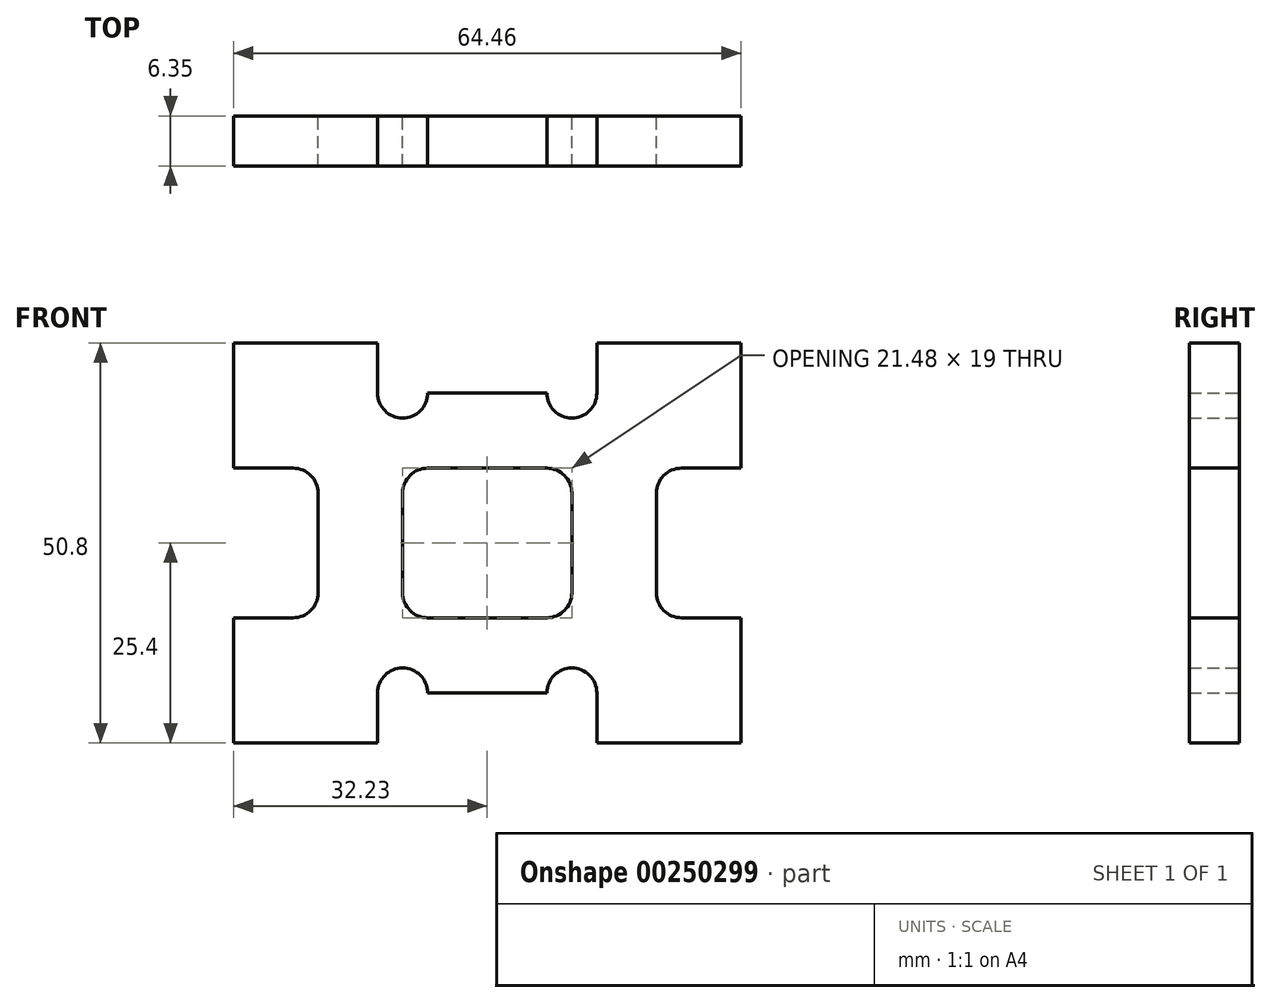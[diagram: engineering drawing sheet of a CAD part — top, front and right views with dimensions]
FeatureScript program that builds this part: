
annotation { "Feature Type Name" : "Feature", "Feature Type Description" : "" }
export const myFeature = defineFeature(function(context is Context, id is Id, definition is map)
    precondition{}
    {
        {
            var Q0;
            Q0=qCreatedBy(makeId("Front.planeOp"),FACE);
            var sketch = newSketch(context, id + "F0", { "sketchPlane" : qUnion([Q0])});
            skLineSegment(sketch, "E0", {"start": v(-13.92, -19.05) * mm, "end": v(-13.92, -25.4) * mm});
            skArc(sketch, "E1", {"start": v(-7.57, -19.05) * mm, "mid": v(-10.74, -15.88) * mm, "end": v(-13.92, -19.05) * mm});
            skLineSegment(sketch, "E2", {"start": v(7.57, -19.05) * mm, "end": v(-7.57, -19.05) * mm});
            skArc(sketch, "E3", {"start": v(13.92, -19.05) * mm, "mid": v(10.74, -15.88) * mm, "end": v(7.57, -19.05) * mm});
            skLineSegment(sketch, "E4", {"start": v(13.92, -25.4) * mm, "end": v(13.92, -19.05) * mm});
            skLineSegment(sketch, "E5", {"start": v(32.23, -25.4) * mm, "end": v(13.92, -25.4) * mm});
            skLineSegment(sketch, "E6", {"start": v(32.23, -9.5) * mm, "end": v(32.23, -25.4) * mm});
            skLineSegment(sketch, "E7", {"start": v(24.66, -9.5) * mm, "end": v(32.23, -9.5) * mm});
            skArc(sketch, "E8", {"start": v(21.48, -6.32) * mm, "mid": v(22.41, -8.57) * mm, "end": v(24.66, -9.5) * mm});
            skArc(sketch, "E9", {"start": v(24.66, 9.5) * mm, "mid": v(22.41, 8.57) * mm, "end": v(21.48, 6.32) * mm});
            skLineSegment(sketch, "E10", {"start": v(32.23, 9.5) * mm, "end": v(24.66, 9.5) * mm});
            skLineSegment(sketch, "E11", {"start": v(32.23, 25.4) * mm, "end": v(32.23, 9.5) * mm});
            skLineSegment(sketch, "E12", {"start": v(13.92, 25.4) * mm, "end": v(32.23, 25.4) * mm});
            skLineSegment(sketch, "E13", {"start": v(13.92, 19.05) * mm, "end": v(13.92, 25.4) * mm});
            skArc(sketch, "E14", {"start": v(7.57, 19.05) * mm, "mid": v(10.74, 15.88) * mm, "end": v(13.92, 19.05) * mm});
            skLineSegment(sketch, "E15", {"start": v(-7.57, 19.05) * mm, "end": v(7.57, 19.05) * mm});
            skArc(sketch, "E16", {"start": v(-13.92, 19.05) * mm, "mid": v(-10.74, 15.88) * mm, "end": v(-7.57, 19.05) * mm});
            skLineSegment(sketch, "E17", {"start": v(-13.92, 25.4) * mm, "end": v(-13.92, 19.05) * mm});
            skLineSegment(sketch, "E18", {"start": v(-32.23, 25.4) * mm, "end": v(-13.92, 25.4) * mm});
            skLineSegment(sketch, "E19", {"start": v(-32.23, 9.5) * mm, "end": v(-32.23, 25.4) * mm});
            skLineSegment(sketch, "E20", {"start": v(-32.23, -25.4) * mm, "end": v(-32.23, -9.5) * mm});
            skLineSegment(sketch, "E21", {"start": v(-13.92, -25.4) * mm, "end": v(-32.23, -25.4) * mm});
            skLineSegment(sketch, "E22", {"start": v(7.57, 9.5) * mm, "end": v(-7.57, 9.5) * mm});
            skLineSegment(sketch, "E23", {"start": v(-7.57, -9.5) * mm, "end": v(7.57, -9.5) * mm});
            skArc(sketch, "E24", {"start": v(-10.74, -6.32) * mm, "mid": v(-9.81, -8.57) * mm, "end": v(-7.57, -9.5) * mm});
            skArc(sketch, "E25", {"start": v(7.57, -9.5) * mm, "mid": v(9.81, -8.57) * mm, "end": v(10.74, -6.32) * mm});
            skArc(sketch, "E26", {"start": v(10.74, 6.32) * mm, "mid": v(9.81, 8.57) * mm, "end": v(7.57, 9.5) * mm});
            skArc(sketch, "E27", {"start": v(-7.57, 9.5) * mm, "mid": v(-9.81, 8.57) * mm, "end": v(-10.74, 6.32) * mm});
            skLineSegment(sketch, "E28", {"start": v(-24.66, -9.5) * mm, "end": v(-32.23, -9.5) * mm});
            skLineSegment(sketch, "E29", {"start": v(-32.23, 9.5) * mm, "end": v(-24.66, 9.5) * mm});
            skArc(sketch, "E30", {"start": v(-24.66, -9.5) * mm, "mid": v(-22.41, -8.57) * mm, "end": v(-21.48, -6.32) * mm});
            skArc(sketch, "E31", {"start": v(-21.48, 6.32) * mm, "mid": v(-22.41, 8.57) * mm, "end": v(-24.66, 9.5) * mm});
            skLineSegment(sketch, "E32", {"start": v(21.48, 6.32) * mm, "end": v(21.48, -6.32) * mm});
            skLineSegment(sketch, "E33", {"start": v(-21.48, 6.32) * mm, "end": v(-21.48, -6.32) * mm});
            skLineSegment(sketch, "E34", {"start": v(-10.74, 6.32) * mm, "end": v(-10.74, -6.32) * mm});
            skLineSegment(sketch, "E35", {"start": v(10.74, 6.32) * mm, "end": v(10.74, -6.32) * mm});
            skSolve(sketch);
        }
        {
            var Q0;
            Q0=makeQuery(id+"F0.imprint","IMPRINT",FACE,{"disambiguationData":[TD([[makeQuery(id+"F0.imprint","IMPRINT",EDGE,{"derivedFrom":sQuery(id+"F0.wireOp",EDGE,"E0")}),-1.0]])]});
            extrude(context, id + "F1", {"entities" : qUnion([Q0]), "depth" : 6.35 * mm});
        }
    });
